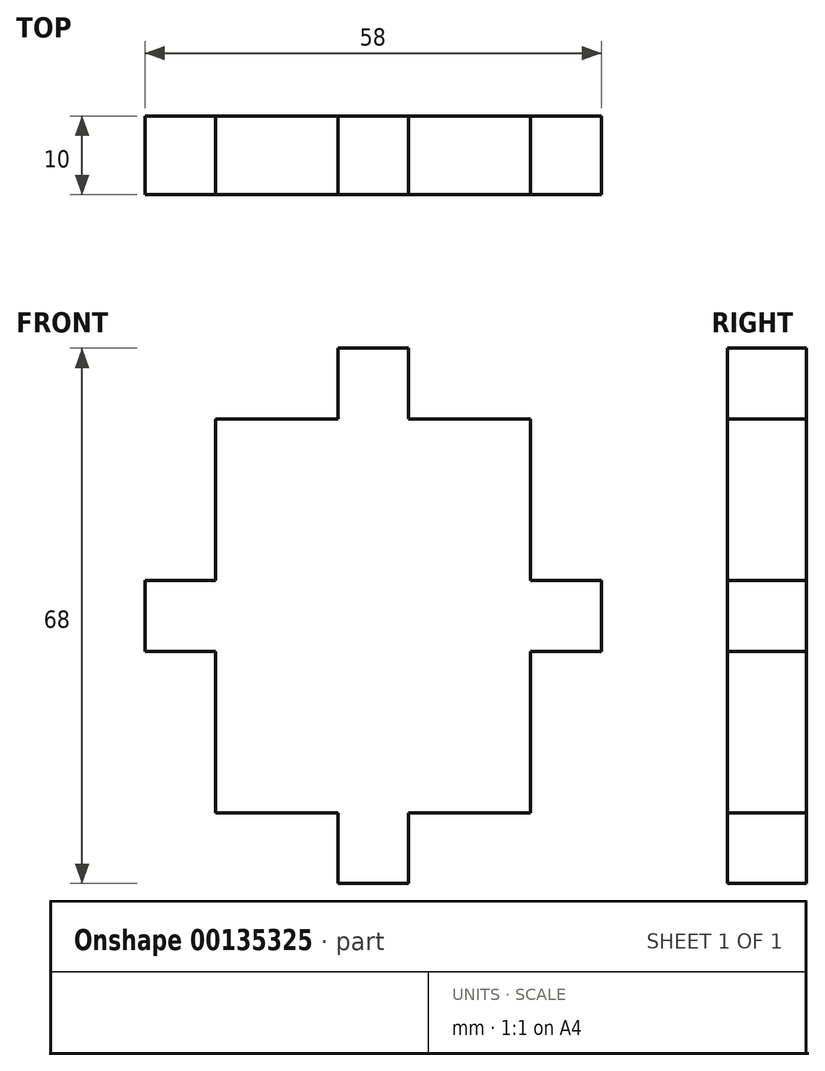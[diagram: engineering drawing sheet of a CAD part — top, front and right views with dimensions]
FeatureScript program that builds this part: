
annotation { "Feature Type Name" : "Feature", "Feature Type Description" : "" }
export const myFeature = defineFeature(function(context is Context, id is Id, definition is map)
    precondition{}
    {
        {
            var Q0;
            Q0=qCreatedBy(makeId("Front.planeOp"),FACE);
            var sketch = newSketch(context, id + "F0", { "sketchPlane" : qUnion([Q0])});
            skLineSegment(sketch, "E0.bottom", {"start": v(-36.69, 50) * mm, "end": v(3.31, 50) * mm});
            skLineSegment(sketch, "E0.top", {"start": v(-36.69, 0) * mm, "end": v(3.31, 0) * mm});
            skLineSegment(sketch, "E0.left", {"start": v(-36.69, 50) * mm, "end": v(-36.69, 0) * mm});
            skLineSegment(sketch, "E0.right", {"start": v(3.31, 50) * mm, "end": v(3.31, 0) * mm});
            skLineSegment(sketch, "E1.left", {"start": v(-36.69, 50) * mm, "end": v(-36.69, 50) * mm});
            skLineSegment(sketch, "E1.right", {"start": v(3.31, 50) * mm, "end": v(3.31, 50) * mm});
            skLineSegment(sketch, "E2.bottom", {"start": v(3.31, 50) * mm, "end": v(-36.69, 50) * mm});
            skLineSegment(sketch, "E2.top", {"start": v(3.31, 50) * mm, "end": v(-36.69, 50) * mm});
            skLineSegment(sketch, "E3.bottom", {"start": v(3.31, 29.5) * mm, "end": v(12.31, 29.5) * mm});
            skLineSegment(sketch, "E3.top", {"start": v(3.31, 20.5) * mm, "end": v(12.31, 20.5) * mm});
            skLineSegment(sketch, "E3.left", {"start": v(3.31, 29.5) * mm, "end": v(3.31, 20.5) * mm});
            skLineSegment(sketch, "E3.right", {"start": v(12.31, 29.5) * mm, "end": v(12.31, 20.5) * mm});
            skLineSegment(sketch, "E4.bottom", {"start": v(-21.19, 0) * mm, "end": v(-12.19, 0) * mm});
            skLineSegment(sketch, "E4.top", {"start": v(-21.19, -9) * mm, "end": v(-12.19, -9) * mm});
            skLineSegment(sketch, "E4.left", {"start": v(-21.19, 0) * mm, "end": v(-21.19, -9) * mm});
            skLineSegment(sketch, "E4.right", {"start": v(-12.19, 0) * mm, "end": v(-12.19, -9) * mm});
            skLineSegment(sketch, "E5", {"start": v(-16.69, 50) * mm, "end": v(-16.69, -39.94) * mm, "construction": true});
            skLineSegment(sketch, "E6.MirrorCS", {"start": v(-36.69, 29.5) * mm, "end": v(-45.69, 29.5) * mm});
            skLineSegment(sketch, "E7.MirrorCS", {"start": v(-45.69, 29.5) * mm, "end": v(-45.69, 20.5) * mm});
            skLineSegment(sketch, "E8.MirrorCS", {"start": v(-36.69, 20.5) * mm, "end": v(-45.69, 20.5) * mm});
            skLineSegment(sketch, "E9", {"start": v(-36.69, 25) * mm, "end": v(-1.13, 25) * mm, "construction": true});
            skPoint(sketch, "E9.endSnap0", {"position": v(3.31, 25) * mm});
            skLineSegment(sketch, "E10.MirrorCS", {"start": v(-21.19, 50) * mm, "end": v(-21.19, 59) * mm});
            skLineSegment(sketch, "E11.MirrorCS", {"start": v(-21.19, 59) * mm, "end": v(-12.19, 59) * mm});
            skLineSegment(sketch, "E12.MirrorCS", {"start": v(-12.19, 50) * mm, "end": v(-12.19, 59) * mm});
            skSolve(sketch);
        }
        {
            var Q0;
            Q0 = qSketchRegion(id + "F0", true);
            extrude(context, id + "F1", {"entities" : qUnion([Q0]), "depth" : 10 * mm});
        }
    });
